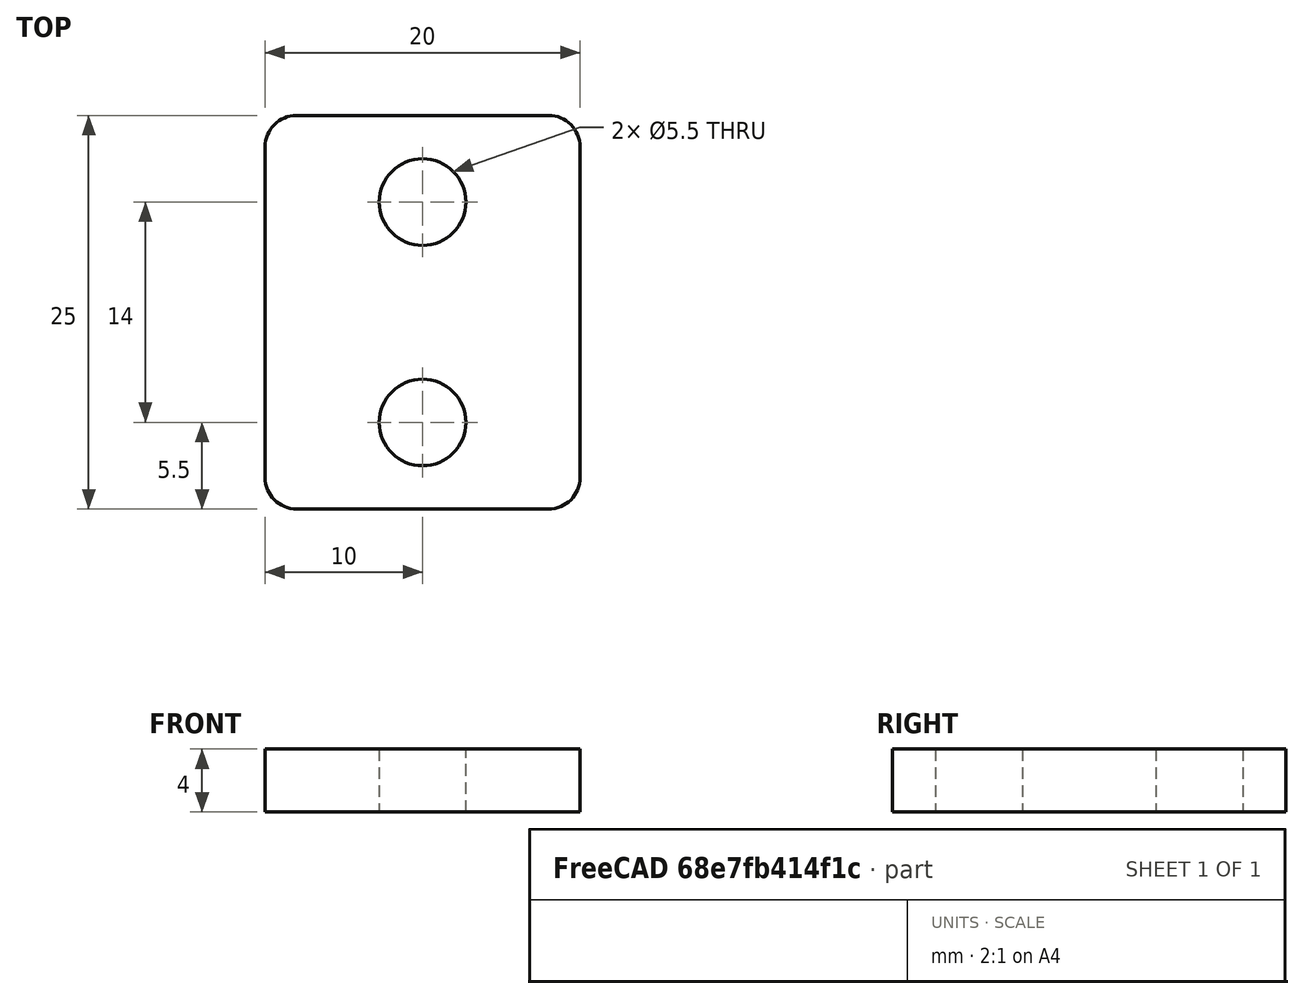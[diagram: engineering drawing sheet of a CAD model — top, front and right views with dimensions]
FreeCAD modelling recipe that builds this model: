
FCSTD DOCUMENT  (FreeCAD 0.19R24267 +99 (Git))
Label: V2 Clamp elastic retaining plate 2 holes
License: All rights reserved
LicenseURL: http://en.wikipedia.org/wiki/All_rights_reserved
objects: Sketcher::SketchObject×1, PartDesign::Pad×1, PartDesign::Body×1
note: 4 computed .brp shape members not serialized (recipe doc carries the construction recipe); baked Part::Feature solids carry a one-line shape summary decoded from their .brp

FEATURE [Sketcher::SketchObject] Sketch
  FullyConstrained = true
  MapMode = 5
  Support = -> [XY_Plane]
  sketch-geometry (11):
    g0: LineSegment StartX=2 StartY=12.5 StartZ=0 EndX=18 EndY=12.5 EndZ=0
    g1: LineSegment StartX=20 StartY=10.5 StartZ=0 EndX=20 EndY=-10.5 EndZ=0
    g2: LineSegment StartX=18 StartY=-12.5 StartZ=0 EndX=2 EndY=-12.5 EndZ=0
    g3: LineSegment StartX=0 StartY=-10.5 StartZ=0 EndX=0 EndY=10.5 EndZ=0
    g4: ArcOfCircle CenterX=2 CenterY=10.5 CenterZ=0 NormalX=0 NormalY=0 NormalZ=1 AngleXU=0 Radius=2 StartAngle=1.5708 EndAngle=3.14159
    g5: ArcOfCircle CenterX=2 CenterY=-10.5 CenterZ=0 NormalX=0 NormalY=0 NormalZ=1 AngleXU=0 Radius=2 StartAngle=3.14159 EndAngle=4.71239
    g6: ArcOfCircle CenterX=18 CenterY=-10.5 CenterZ=0 NormalX=0 NormalY=0 NormalZ=1 AngleXU=0 Radius=2 StartAngle=4.71239 EndAngle=6.28319
    g7: ArcOfCircle CenterX=18 CenterY=10.5 CenterZ=0 NormalX=0 NormalY=0 NormalZ=1 AngleXU=0 Radius=2 StartAngle=1e-16 EndAngle=1.5708
    g8: Circle CenterX=10 CenterY=-7 CenterZ=0 NormalX=0 NormalY=0 NormalZ=1 AngleXU=0 Radius=2.75
    g9: Circle CenterX=10 CenterY=7 CenterZ=0 NormalX=0 NormalY=0 NormalZ=1 AngleXU=0 Radius=2.75
    g10: LineSegment StartX=10 StartY=7 StartZ=0 EndX=10 EndY=-7 EndZ=0
  constraints (26):
    c: Horizontal(g0)
    c: Horizontal(g2)
    c: Vertical(g1)
    c: Tangent(g3,g4) = 1.5708
    c: Tangent(g0,g4) = 1.5708
    c: Tangent(g3,g5) = 1.5708
    c: Tangent(g2,g5) = 1.5708
    c: Tangent(g2,g6) = 1.5708
    c: Tangent(g0,g7) = 1.5708
    c: DistanceY(g2,g0) = 25
    c: Symmetric(g0,g2,g-1)
    c: Vertical(g3)
    c: Equal(g7,g6)
    c: Radius(g4) = 2
    c: Coincident(g10,g9)
    c: Coincident(g10,g8)
    c: DistanceX(g3,g8) = 10
    c: PointOnObject(g-1,g3)
    c: Equal(g9,g8)
    c: DistanceY(g10,g10) = 14
    c: Symmetric(g9,g8,g-1)
    c: Equal(g7,g4)
    c: DistanceX(g8,g1) = 10
    c: Tangent(g7,g1) = 1.5708
    c: Tangent(g1,g6) = 1.5708
    c: Diameter(g9) = 5.5
FEATURE [PartDesign::Pad] Pad  label="Plate thickness"
  Direction = (1,1,1)
  Length = 4
  Length2 = 100
  Profile = -> Sketch
  Type = 0
FEATURE [PartDesign::Body] Body
  Group = -> [Sketch,Pad]
  Origin = -> Origin
  Tip = -> Pad
